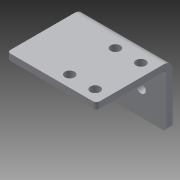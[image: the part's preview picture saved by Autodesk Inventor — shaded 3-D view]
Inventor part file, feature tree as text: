
AUTODESK INVENTOR PART (.ipt)
format: ipt  version: 2014 (Build 180170000, 170)  size: 171,008 bytes
history: native  units: in
note: dims shown in document units (in); Inventor stores cm internally (conversion verified against a paired STEP export)
features: sheet_metal_op x4, sketch x3, other x3, fillet x1, extrude x1
ambient origin geometry x8: Origin, YZ Plane, XZ Plane, XY Plane, X Axis, Y Axis, Z Axis, Center Point
bodies: Solid1 (feature_tree)
feature tree (12):
  sheet_metal_op  "Face1"
  sheet_metal_op  "Flange1"
  fillet  "Fillet1"  Radius=1.75in
  extrude  "Extrusion1"  Depth=0.19in
  sketch  "Sketch1"  dims[d1=1.0in d2=0.19in]
  other  "Plate1"
  sketch  "Sketch2"  dims[d4=0.7874in d6=1.0in d7=0.3937in d9=1.0in]
  other  "Plate2"
  sheet_metal_op  "Bend1"
  sheet_metal_op  "Corner1"
  sketch  "Sketch3"  dims[d11=0.125in d12=0.125in d13=0.0625in d14=0.25in d15=0.125in d16=1.5in d17=90.0deg d18=0.05in d19=0.5in d20=0.125in d21=0.125in d22=0.0625in d23=1.35in d24=0.75in d27=0.19in d28=0.125in d29=0.2265in d30=1.0in d31=0.0in d34=0.25in d35=0.875in]
  other  "Definition1"
